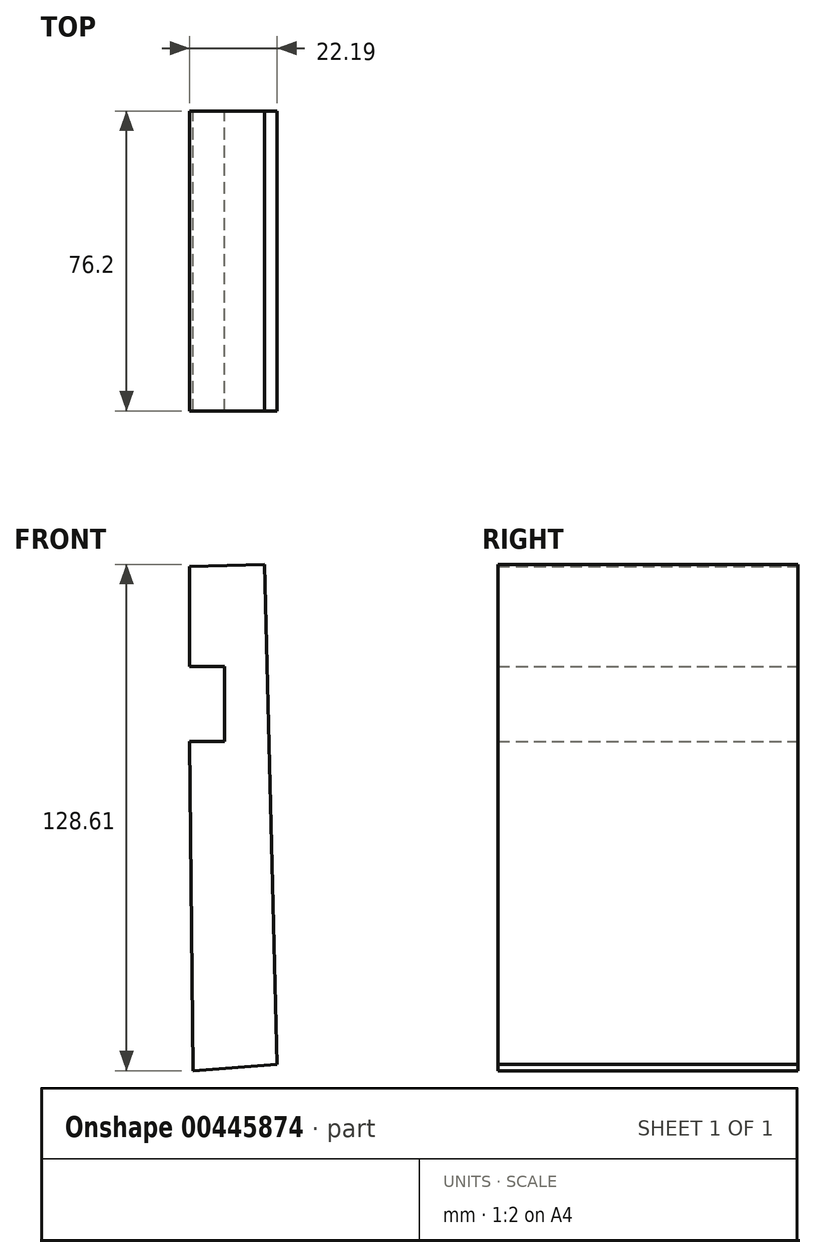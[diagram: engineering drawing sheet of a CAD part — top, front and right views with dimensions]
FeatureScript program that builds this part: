
annotation { "Feature Type Name" : "Feature", "Feature Type Description" : "" }
export const myFeature = defineFeature(function(context is Context, id is Id, definition is map)
    precondition{}
    {
        {
            var Q0;
            Q0=qCreatedBy(makeId("Front.planeOp"),FACE);
            var sketch = newSketch(context, id + "F0", { "sketchPlane" : qUnion([Q0])});
            skLineSegment(sketch, "E0", {"start": v(21.29, -63.89) * mm, "end": v(18.14, 63.07) * mm});
            skLineSegment(sketch, "E1", {"start": v(18.14, 63.07) * mm, "end": v(-0.9, 62.6) * mm});
            skLineSegment(sketch, "E2", {"start": v(-0.9, 62.6) * mm, "end": v(-0.9, 37.2) * mm});
            skLineSegment(sketch, "E3", {"start": v(-0.9, 37.2) * mm, "end": v(7.95, 37.2) * mm});
            skLineSegment(sketch, "E4", {"start": v(7.95, 37.2) * mm, "end": v(7.95, 18.15) * mm});
            skLineSegment(sketch, "E5", {"start": v(7.95, 18.15) * mm, "end": v(-0.9, 18.15) * mm});
            skLineSegment(sketch, "E6", {"start": v(-0.9, 18.15) * mm, "end": v(0, -65.54) * mm});
            skLineSegment(sketch, "E7", {"start": v(0, -65.54) * mm, "end": v(21.29, -63.89) * mm});
            skSolve(sketch);
        }
        {
            var Q0;
            Q0 = qSketchRegion(id + "F0", true);
            extrude(context, id + "F1", {"entities" : qUnion([Q0]), "depth" : 76.2 * mm});
        }
    });
